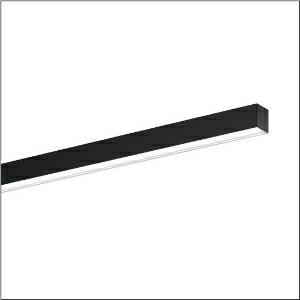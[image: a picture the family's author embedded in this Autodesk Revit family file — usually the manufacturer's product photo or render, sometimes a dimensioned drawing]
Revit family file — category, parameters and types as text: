
# Revit family: silica_r__21_51mx23da44bb_c0fe
name_source: partatom
category: Lighting Fixtures
units: mm (PartAtom-declared; Revit-internal decimal feet)

## family parameters
Cut with Voids When Loaded = No
Host = Face
Light Source = No
Part Type = Normal
Room Calculation Point = No
Round Connector Dimension = Use Diameter
Shared = No

## types (1)
- --- (1 x LED, 3280 lm, 22.4 W, 4000K)
    Apparent Load = 22 VA
    CIE Flux Codes = 78 96 99 100 100
    Color Rendering = 80
    Color Temperature = 4000K
    Default Elevation = 1800 mm
    Description = Silica® 21, office luminaire, primary optical cover: prismatic diffuser, of PMMA, CAT 2 (L<= 3000cd/m²), light emission: direct distribution, primary light characteristic: symmetric, installation type: surface-mounted, LED, rated luminous flux: 3.280lm, luminous efficacy: 146lm/W, light colour: 840, colour temperature: 4000K, control gear: DALI 2, with terminal, 3+2-pole, max. 2.5mm², mains connection: 220..240V, AC, 50/60Hz, rated input power: 22.4W, luminaire housing, of aluminium, matt jet black (RAL 9005), length: 1.204mm, width: 53mm, height: 53mm, protection rating (complete): IP20, insulation class (complete): insulation class I (protective earthing), certification: CE, permissible operating ambient temperature: 0..+35°C, standard: EN 50419, packaging unit: 1 piece
    Height = 53 mm
    Lamp = 1 x LED
    Lamp Light Flux = 3280 lm
    Lamp Power = 22.4 W
    Lamp count = 1
    Length = 1204 mm
    Luminous efficacy = 146 lm/W
    Manufacturer = Siteco
    ModVariant = No
    Model = 51MX23DA44BB
    Mounting Place = Ceiling
    Mounting Type = Surface mounted
    Number of Poles = 1
    OnlyDefault = Yes
    Power Factor = 1
    Product Name = Silica® 21
    Product group = office luminaire | ceiling mounted
    ProductGroupID = 303
    Protection Class = Protection class I
    Protection Degree = IP 20
    RLX_Detail_Level = 1
    RLX_Emergency_Light_Flux = 0 lm
    RLX_Emergency_Type = 0
    RLX_Emergency_Type_DB = No
    RlxData = <blob elided: 23733 chars, md5=c8cc38b8>
    Socket = socket
    Standby Power = 0 W
    System Light Flux = 3280 lm
    System Power = 22 W
    Type Comments = factory setting: luminous flux: 100 % | dim-lin: 254 | 323 mA
    Type Image = l_1335925.jpg
    URL = http://relux.com
    VarID = @adj_027077
    Voltage = 0 V
    Weight = 0.00 kg
    Width = 53 mm

## geometry (parser evidence)
native form markers: Blend x4, Sweep x11
no freeform markers — native parametric forms only
